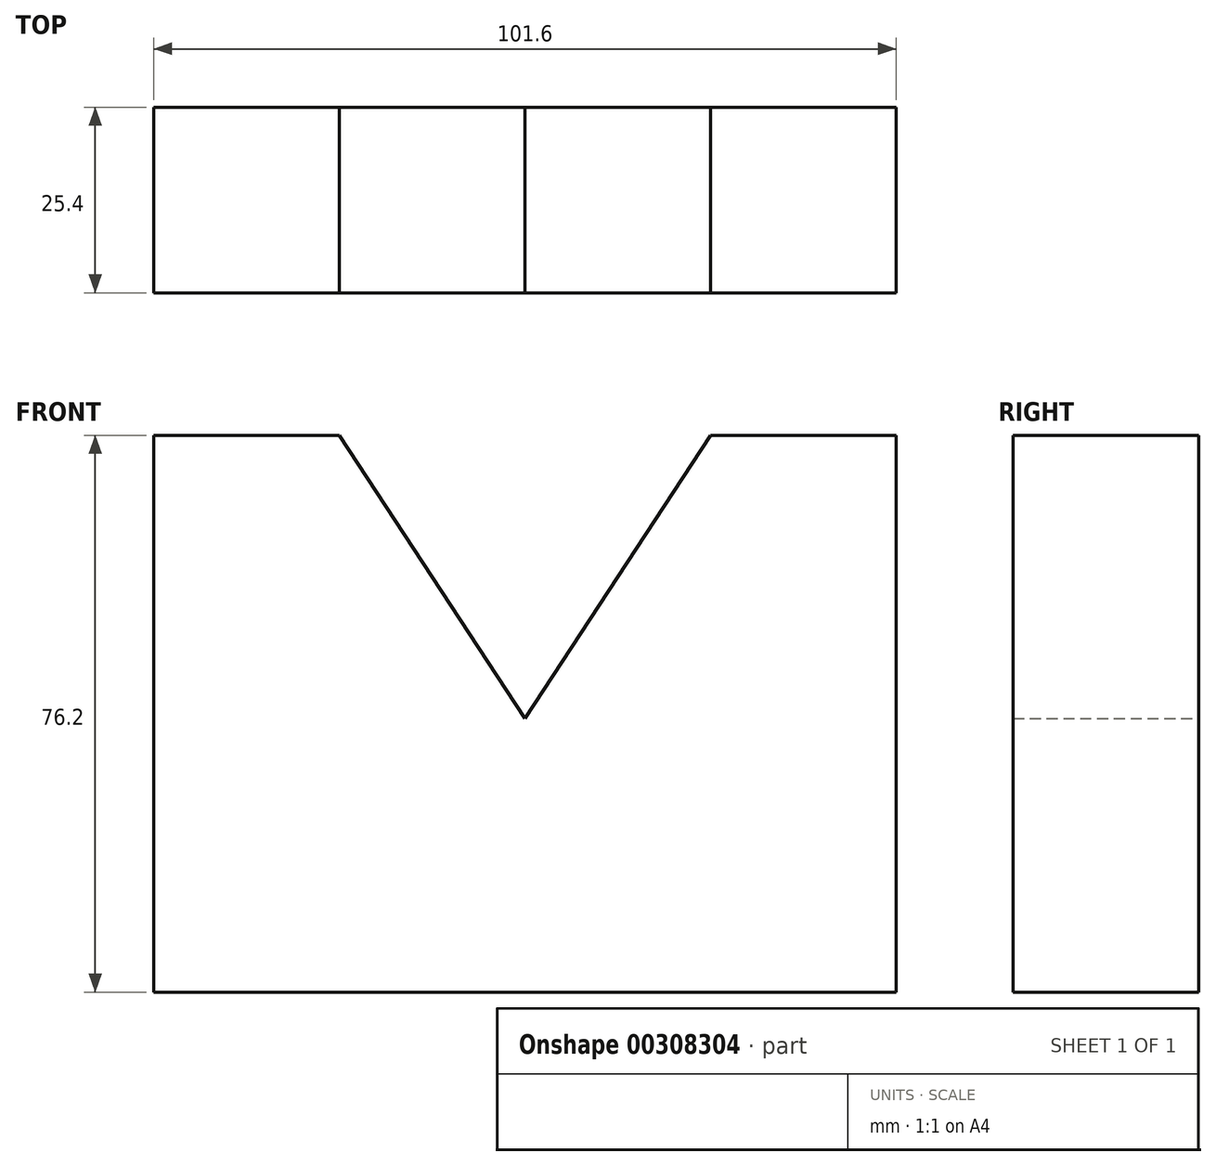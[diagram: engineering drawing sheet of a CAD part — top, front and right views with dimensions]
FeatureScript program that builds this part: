
annotation { "Feature Type Name" : "Feature", "Feature Type Description" : "" }
export const myFeature = defineFeature(function(context is Context, id is Id, definition is map)
    precondition{}
    {
        {
            var Q0;
            Q0=qCreatedBy(makeId("Front.planeOp"),FACE);
            var sketch = newSketch(context, id + "F0", { "sketchPlane" : qUnion([Q0])});
            skLineSegment(sketch, "E0", {"start": v(-47.82, -26.95) * mm, "end": v(53.78, -26.95) * mm});
            skLineSegment(sketch, "E1", {"start": v(-47.82, -26.95) * mm, "end": v(-47.82, 49.25) * mm});
            skLineSegment(sketch, "E2", {"start": v(-47.82, 49.25) * mm, "end": v(-22.42, 49.25) * mm});
            skLineSegment(sketch, "E3", {"start": v(28.38, 49.25) * mm, "end": v(53.78, 49.25) * mm});
            skLineSegment(sketch, "E4", {"start": v(53.78, 49.25) * mm, "end": v(53.78, -26.95) * mm});
            skLineSegment(sketch, "E5", {"start": v(2.98, 10.5) * mm, "end": v(-22.42, 49.25) * mm});
            skLineSegment(sketch, "E6", {"start": v(28.38, 49.25) * mm, "end": v(2.98, 10.5) * mm});
            skSolve(sketch);
        }
        {
            var Q0;
            Q0=makeQuery(id+"F0.imprint","IMPRINT",FACE,{"disambiguationData":[TD([[makeQuery(id+"F0.imprint","IMPRINT",EDGE,{"derivedFrom":sQuery(id+"F0.wireOp",EDGE,"E0")}),1.0]])]});
            extrude(context, id + "F1", {"entities" : qUnion([Q0]), "depth" : 25.4 * mm});
        }
    });
